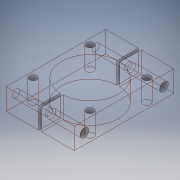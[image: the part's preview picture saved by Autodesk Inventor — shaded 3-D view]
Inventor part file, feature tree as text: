
AUTODESK INVENTOR PART (.ipt)
format: ipt  version: 2018 (Build 220112000, 112)  size: 152,576 bytes
history: native  units: in
note: dims shown in document units (in); Inventor stores cm internally (conversion verified against a paired STEP export)
features: sketch x4, hole x3, extrude x1
ambient origin geometry x8: Origin, YZ Plane, XZ Plane, XY Plane, X Axis, Y Axis, Z Axis, Center Point
bodies: Body1 (feature_tree)
feature tree (8):
  extrude  "Extrusion6"  Depth=1.2in
  hole  "Hole3"  [1 undecoded]
  hole  "Hole4"  [1 undecoded]
  hole  "Hole5"  [1 undecoded]
  sketch  "Sketch8"  dims[d34=1.0in d35=1.2in]
  sketch  "Sketch9"  dims[d36=1.75in d37=0.05in]
  sketch  "Sketch10"  dims[d38=0.375in d39=0.0in d40=1.4in]
  sketch  "Sketch11"  dims[d41=0.375in d42=0.15in d43=0.328in d44=0.279in d45=0.25in d46=0.5635in d47=0.484in d48=0.8108in d49=0.13in d50=0.328in d51=0.279in d52=0.25in d53=0.5635in d54=0.484in d55=0.8108in d56=1.0in d57=1.0in d58=0.13in d59=0.328in d60=0.279in d61=0.25in d62=0.5635in d63=0.484in d64=0.8108in]
note: 3 required parameter values undecoded (feature->parameter linkage not recoverable at this tier; creation-order binding heuristic only, values carry confidence <= 0.55)
